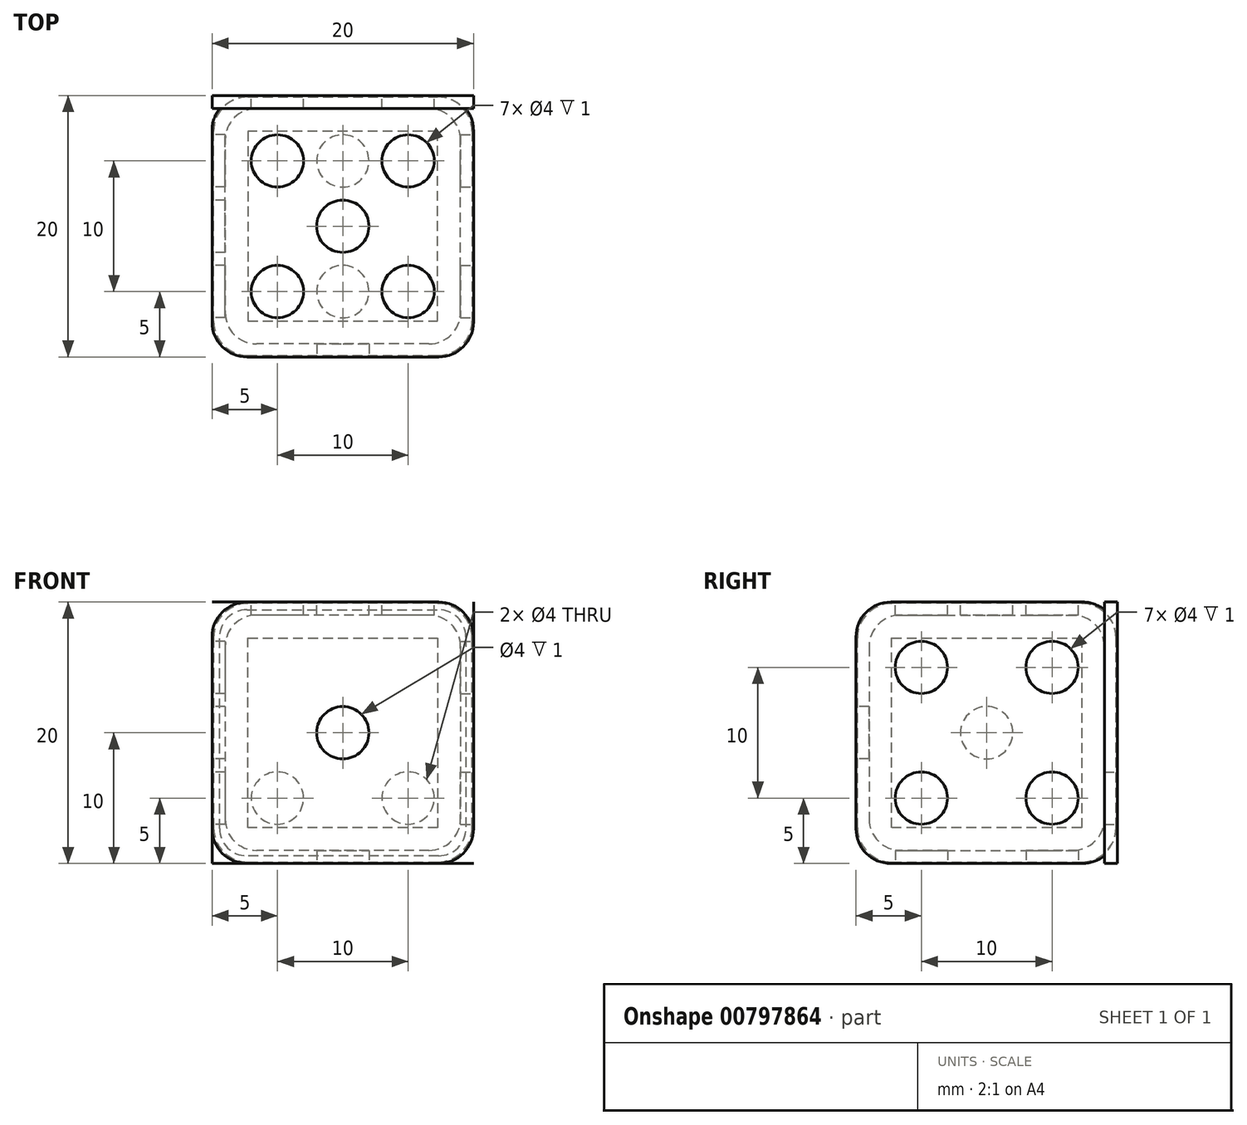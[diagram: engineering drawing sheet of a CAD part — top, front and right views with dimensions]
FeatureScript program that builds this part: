
annotation { "Feature Type Name" : "Feature", "Feature Type Description" : "" }
export const myFeature = defineFeature(function(context is Context, id is Id, definition is map)
    precondition{}
    {
        {
            assignVariable(context, id + "F0", {"variableType" : VariableType.NUMBER, "name" : "prick", "numberValue" : 4});
        }
        {
            assignVariable(context, id + "F1", {"variableType" : VariableType.LENGTH, "name" : "dist", "lengthValue" : ((getVariable(context, 'prick') + 1) * 2) * mm});
        }
        {
            var Q0;
            Q0=qCreatedBy(makeId("Top.planeOp"),FACE);
            var sketch = newSketch(context, id + "F2", { "sketchPlane" : qUnion([Q0])});
            skLineSegment(sketch, "E0.bottom", {"start": v(10, -10) * mm, "end": v(-10, -10) * mm});
            skLineSegment(sketch, "E0.top", {"start": v(10, 10) * mm, "end": v(-10, 10) * mm});
            skLineSegment(sketch, "E0.left", {"start": v(10, -10) * mm, "end": v(10, 10) * mm});
            skLineSegment(sketch, "E0.right", {"start": v(-10, -10) * mm, "end": v(-10, 10) * mm});
            skPoint(sketch, "E0.middle", {"position": v(0, 0) * mm});
            skSolve(sketch);
        }
        {
            var Q0;
            Q0=makeQuery(id+"F2.imprint","IMPRINT",FACE,{"disambiguationData":[TD([[makeQuery(id+"F2.imprint","IMPRINT",EDGE,{"derivedFrom":sQuery(id+"F2.wireOp",EDGE,"E0.bottom")}),-1.0]])]});
            extrude(context, id + "F3", {"entities" : qUnion([Q0]), "endBound" : BoundingType.SYMMETRIC, "depth" : getVariable(context, 'dist') * 2, "offsetDistance" : 25 * mm});
        }
        {
            var Q0;
            Q0=makeQuery(id+"F3.opExtrude","SWEPT_FACE",FACE,{"disambiguationData":[OSD([sQuery(id+"F2.wireOp",EDGE,"E0.bottom")])]});
            var sketch = newSketch(context, id + "F4", { "sketchPlane" : qUnion([Q0])});
            skCircle(sketch, "E1", {"center": v(0, 0) * mm, "radius": 2 * mm});
            skPoint(sketch, "E1.centerSnap0", {"position": v(10, 0) * mm});
            skSolve(sketch);
        }
        {
            var Q0;
            Q0=makeQuery(id+"F4.imprint","IMPRINT",FACE,{"disambiguationData":[TD([[makeQuery(id+"F4.imprint","IMPRINT",EDGE,{"derivedFrom":sQuery(id+"F4.wireOp",EDGE,"E1")}),1.0]])]});
            extrude(context, id + "F5", {"entities" : qUnion([Q0]), "oppositeDirection" : true, "depth" : 1 * mm, "offsetDistance" : 25 * mm});
        }
        {
            var Q0;
            Q0=makeQuery(id+"F3.opExtrude","SWEPT_FACE",FACE,{"disambiguationData":[OSD([sQuery(id+"F2.wireOp",EDGE,"E0.top")])]});
            var sketch = newSketch(context, id + "F6", { "sketchPlane" : qUnion([Q0])});
            skLineSegment(sketch, "E2", {"start": v(5, 0) * mm, "end": v(-5, 0) * mm, "construction": true});
            skPoint(sketch, "E2.startSnap0", {"position": v(10, 0) * mm});
            skPoint(sketch, "E3", {"position": v(0, 0) * mm});
            skCircle(sketch, "E4", {"center": v(-5, 0) * mm, "radius": 2 * mm});
            skCircle(sketch, "E5", {"center": v(5, 0) * mm, "radius": 2 * mm});
            skLineSegment(sketch, "E6.0.1.0", {"start": v(5, 5) * mm, "end": v(-5, 5) * mm, "construction": true});
            skCircle(sketch, "E6.0.1.1", {"center": v(-5, 5) * mm, "radius": 2 * mm});
            skCircle(sketch, "E6.0.1.2", {"center": v(5, 5) * mm, "radius": 2 * mm});
            skLineSegment(sketch, "E6.direction1", {"start": v(-5, 0) * mm, "end": v(35.29, 0) * mm, "construction": true});
            skLineSegment(sketch, "E6.direction2", {"start": v(-5, 0) * mm, "end": v(-5, 5) * mm, "construction": true});
            skCircle(sketch, "E7.MirrorC", {"center": v(5, -5) * mm, "radius": 2 * mm});
            skCircle(sketch, "E8.MirrorC", {"center": v(-5, -5) * mm, "radius": 2 * mm});
            skSolve(sketch);
        }
        {
            var Q0;
            Q0=makeQuery(id+"F6.imprint","IMPRINT",FACE,{"disambiguationData":[TD([[makeQuery(id+"F6.imprint","IMPRINT",EDGE,{"derivedFrom":sQuery(id+"F6.wireOp",EDGE,"E8.MirrorC")}),-1.0]])]});
            var Q1;
            Q1=makeQuery(id+"F6.imprint","IMPRINT",FACE,{"disambiguationData":[TD([[makeQuery(id+"F6.imprint","IMPRINT",EDGE,{"derivedFrom":sQuery(id+"F6.wireOp",EDGE,"E7.MirrorC")}),-1.0]])]});
            var Q2;
            Q2=makeQuery(id+"F6.imprint","IMPRINT",FACE,{"disambiguationData":[TD([[makeQuery(id+"F6.imprint","IMPRINT",EDGE,{"derivedFrom":sQuery(id+"F6.wireOp",EDGE,"E5")}),1.0]])]});
            var Q3;
            Q3=makeQuery(id+"F6.imprint","IMPRINT",FACE,{"disambiguationData":[TD([[makeQuery(id+"F6.imprint","IMPRINT",EDGE,{"derivedFrom":sQuery(id+"F6.wireOp",EDGE,"E4")}),1.0]])]});
            var Q4;
            Q4=makeQuery(id+"F6.imprint","IMPRINT",FACE,{"disambiguationData":[TD([[makeQuery(id+"F6.imprint","IMPRINT",EDGE,{"derivedFrom":sQuery(id+"F6.wireOp",EDGE,"E6.0.1.1")}),1.0]])]});
            var Q5;
            Q5=makeQuery(id+"F6.imprint","IMPRINT",FACE,{"disambiguationData":[TD([[makeQuery(id+"F6.imprint","IMPRINT",EDGE,{"derivedFrom":sQuery(id+"F6.wireOp",EDGE,"E6.0.1.2")}),1.0]])]});
            extrude(context, id + "F7", {"entities" : qUnion([Q0, Q1, Q2, Q3, Q4, Q5]), "oppositeDirection" : true, "depth" : 1 * mm, "offsetDistance" : 25 * mm});
        }
        {
            var Q0;
            Q0=makeQuery(id+"F3.opExtrude","CAP_EDGE",EDGE,{"disambiguationData":[OSD([sQuery(id+"F2.wireOp",EDGE,"E0.bottom")])],"isStart":true});
            var Q1;
            Q1=makeQuery(id+"F3.opExtrude","CAP_EDGE",EDGE,{"disambiguationData":[OSD([sQuery(id+"F2.wireOp",EDGE,"E0.left")])],"isStart":true});
            var Q2;
            Q2=makeQuery(id+"F3.opExtrude","CAP_EDGE",EDGE,{"disambiguationData":[OSD([sQuery(id+"F2.wireOp",EDGE,"E0.right")])],"isStart":true});
            var Q3;
            Q3=makeQuery(id+"F3.opExtrude","CAP_EDGE",EDGE,{"disambiguationData":[OSD([sQuery(id+"F2.wireOp",EDGE,"E0.top")])],"isStart":true});
            var Q4;
            Q4=makeQuery(id+"F3.opExtrude","SWEPT_EDGE",EDGE,{"disambiguationData":[OSD([sQuery(id+"F2.wireOp",EDGE,"E0.bottom"),sQuery(id+"F2.wireOp",EDGE,"E0.right")])]});
            var Q5;
            Q5=makeQuery(id+"F3.opExtrude","SWEPT_EDGE",EDGE,{"disambiguationData":[OSD([sQuery(id+"F2.wireOp",EDGE,"E0.top"),sQuery(id+"F2.wireOp",EDGE,"E0.right")])]});
            var Q6;
            Q6=makeQuery(id+"F3.opExtrude","SWEPT_EDGE",EDGE,{"disambiguationData":[OSD([sQuery(id+"F2.wireOp",EDGE,"E0.bottom"),sQuery(id+"F2.wireOp",EDGE,"E0.left")])]});
            var Q7;
            Q7=makeQuery(id+"F3.opExtrude","SWEPT_EDGE",EDGE,{"disambiguationData":[OSD([sQuery(id+"F2.wireOp",EDGE,"E0.top"),sQuery(id+"F2.wireOp",EDGE,"E0.left")])]});
            var Q8;
            Q8=makeQuery(id+"F3.opExtrude","CAP_EDGE",EDGE,{"disambiguationData":[OSD([sQuery(id+"F2.wireOp",EDGE,"E0.left")])],"isStart":false});
            var Q9;
            Q9=makeQuery(id+"F3.opExtrude","CAP_EDGE",EDGE,{"disambiguationData":[OSD([sQuery(id+"F2.wireOp",EDGE,"E0.top")])],"isStart":false});
            var Q10;
            Q10=makeQuery(id+"F3.opExtrude","CAP_EDGE",EDGE,{"disambiguationData":[OSD([sQuery(id+"F2.wireOp",EDGE,"E0.bottom")])],"isStart":false});
            var Q11;
            Q11=makeQuery(id+"F3.opExtrude","CAP_EDGE",EDGE,{"disambiguationData":[OSD([sQuery(id+"F2.wireOp",EDGE,"E0.right")])],"isStart":false});
            fillet(context, id + "F8", {"entities" : qUnion([Q0, Q1, Q2, Q3, Q4, Q5, Q6, Q7, Q8, Q9, Q10, Q11]), "tangentPropagation" : true, "radius" : (getVariable(context, 'prick') / 1.5) * mm, "defaultsChanged" : true, "vertexSettings" : [], "allowEdgeOverflow" : false});
        }
        {
            var Q0;
            Q0=makeQuery(id+"F3.opExtrude","CAP_FACE",FACE,{"disambiguationData":[OSD([sQuery(id+"F2.wireOp",EDGE,"E0.bottom"),sQuery(id+"F2.wireOp",EDGE,"E0.top"),sQuery(id+"F2.wireOp",EDGE,"E0.left"),sQuery(id+"F2.wireOp",EDGE,"E0.right")])],"isStart":false});
            var sketch = newSketch(context, id + "F9", { "sketchPlane" : qUnion([Q0])});
            skLineSegment(sketch, "E9.bottom", {"start": v(5, 5) * mm, "end": v(-5, 5) * mm, "construction": true});
            skLineSegment(sketch, "E9.top", {"start": v(5, -5) * mm, "end": v(-5, -5) * mm, "construction": true});
            skLineSegment(sketch, "E9.left", {"start": v(5, 5) * mm, "end": v(5, -5) * mm, "construction": true});
            skLineSegment(sketch, "E9.right", {"start": v(-5, 5) * mm, "end": v(-5, -5) * mm, "construction": true});
            skPoint(sketch, "E9.middle", {"position": v(0, 0) * mm});
            skCircle(sketch, "E10", {"center": v(0, 0) * mm, "radius": 2 * mm});
            skCircle(sketch, "E11", {"center": v(-5, 5) * mm, "radius": 2 * mm});
            skCircle(sketch, "E12", {"center": v(-5, -5) * mm, "radius": 2 * mm});
            skCircle(sketch, "E13", {"center": v(5, -5) * mm, "radius": 2 * mm});
            skCircle(sketch, "E14", {"center": v(5, 5) * mm, "radius": 2 * mm});
            skSolve(sketch);
        }
        {
            var Q0;
            Q0 = qSketchRegion(id + "F9", true);
            extrude(context, id + "F10", {"entities" : qUnion([Q0]), "oppositeDirection" : true, "depth" : 1 * mm, "offsetDistance" : 25 * mm});
        }
        {
            var Q0;
            Q0=makeQuery(id+"F3.opExtrude","CAP_FACE",FACE,{"disambiguationData":[OSD([sQuery(id+"F2.wireOp",EDGE,"E0.bottom"),sQuery(id+"F2.wireOp",EDGE,"E0.top"),sQuery(id+"F2.wireOp",EDGE,"E0.left"),sQuery(id+"F2.wireOp",EDGE,"E0.right")])],"isStart":true});
            var sketch = newSketch(context, id + "F11", { "sketchPlane" : qUnion([Q0])});
            skLineSegment(sketch, "E15", {"start": v(0, -5) * mm, "end": v(0, 5) * mm});
            skCircle(sketch, "E16", {"center": v(0, -5) * mm, "radius": 2 * mm});
            skCircle(sketch, "E17", {"center": v(0, 5) * mm, "radius": 2 * mm});
            skSolve(sketch);
        }
        {
            var Q0;
            Q0=makeQuery(id+"F11.imprint","IMPRINT",FACE,{"disambiguationData":[TD([[makeQuery(id+"F11.imprint","IMPRINT",EDGE,{"derivedFrom":sQuery(id+"F11.wireOp",EDGE,"E16")}),1.0]])]});
            var Q1;
            Q1=makeQuery(id+"F11.imprint","IMPRINT",FACE,{"disambiguationData":[TD([[makeQuery(id+"F11.imprint","IMPRINT",EDGE,{"derivedFrom":sQuery(id+"F11.wireOp",EDGE,"E17")}),1.0]])]});
            extrude(context, id + "F12", {"entities" : qUnion([Q0, Q1]), "oppositeDirection" : true, "depth" : 1 * mm, "offsetDistance" : 25 * mm});
        }
        {
            var Q0;
            Q0=makeQuery(id+"F3.opExtrude","SWEPT_FACE",FACE,{"disambiguationData":[OSD([sQuery(id+"F2.wireOp",EDGE,"E0.right")])]});
            var sketch = newSketch(context, id + "F13", { "sketchPlane" : qUnion([Q0])});
            skLineSegment(sketch, "E18.bottom", {"start": v(5, 5) * mm, "end": v(-5, 5) * mm, "construction": true});
            skLineSegment(sketch, "E18.top", {"start": v(5, -5) * mm, "end": v(-5, -5) * mm, "construction": true});
            skLineSegment(sketch, "E18.left", {"start": v(5, 5) * mm, "end": v(5, -5) * mm, "construction": true});
            skLineSegment(sketch, "E18.right", {"start": v(-5, 5) * mm, "end": v(-5, -5) * mm, "construction": true});
            skPoint(sketch, "E18.middle", {"position": v(0, 0) * mm});
            skPoint(sketch, "E18.middle.positionSnap0", {"position": v(-7.33, 0) * mm});
            skPoint(sketch, "E18.centerSnap0", {"position": v(-7.33, 0) * mm});
            skCircle(sketch, "E19", {"center": v(0, 0) * mm, "radius": 2 * mm});
            skCircle(sketch, "E20", {"center": v(5, 5) * mm, "radius": 2 * mm});
            skCircle(sketch, "E21", {"center": v(-5, -5) * mm, "radius": 2 * mm});
            skSolve(sketch);
        }
        {
            var Q0;
            Q0=makeQuery(id+"F3.opExtrude","SWEPT_FACE",FACE,{"disambiguationData":[OSD([sQuery(id+"F2.wireOp",EDGE,"E0.left")])]});
            var sketch = newSketch(context, id + "F14", { "sketchPlane" : qUnion([Q0])});
            skLineSegment(sketch, "E22.bottom", {"start": v(5, -5) * mm, "end": v(-5, -5) * mm, "construction": true});
            skLineSegment(sketch, "E22.top", {"start": v(5, 5) * mm, "end": v(-5, 5) * mm, "construction": true});
            skLineSegment(sketch, "E22.left", {"start": v(5, -5) * mm, "end": v(5, 5) * mm, "construction": true});
            skLineSegment(sketch, "E22.right", {"start": v(-5, -5) * mm, "end": v(-5, 5) * mm, "construction": true});
            skPoint(sketch, "E22.middle", {"position": v(0, 0) * mm});
            skPoint(sketch, "E22.middle.positionSnap0", {"position": v(7.33, 0) * mm});
            skPoint(sketch, "E22.centerSnap0", {"position": v(7.33, 0) * mm});
            skCircle(sketch, "E23", {"center": v(5, 5) * mm, "radius": 2 * mm});
            skCircle(sketch, "E24", {"center": v(5, -5) * mm, "radius": 2 * mm});
            skCircle(sketch, "E25", {"center": v(-5, -5) * mm, "radius": 2 * mm});
            skCircle(sketch, "E26", {"center": v(-5, 5) * mm, "radius": 2 * mm});
            skSolve(sketch);
        }
        {
            var Q0;
            Q0 = qSketchRegion(id + "F13", true);
            extrude(context, id + "F15", {"entities" : qUnion([Q0]), "oppositeDirection" : true, "depth" : 1 * mm, "offsetDistance" : 25 * mm});
        }
        {
            var Q0;
            Q0 = qSketchRegion(id + "F14", true);
            extrude(context, id + "F16", {"entities" : qUnion([Q0]), "oppositeDirection" : true, "depth" : 1 * mm, "offsetDistance" : 25 * mm});
        }
        {
            var Q0;
            Q0=makeQuery(id+"F3.opExtrude","SWEPT_BODY",BODY,{"disambiguationData":[OSD([sQuery(id+"F2.wireOp",EDGE,"E0.bottom"),sQuery(id+"F2.wireOp",EDGE,"E0.top"),sQuery(id+"F2.wireOp",EDGE,"E0.left"),sQuery(id+"F2.wireOp",EDGE,"E0.right")])]});
            var Q1;
            Q1=qCreatedBy(makeId("Origin.pointOp"),VERTEX);
            transform(context, id + "F17", {"entities" : qUnion([Q0]), "transformType" : TransformType.SCALE_UNIFORMLY, "scale" : 0.99, "scalePoint" : qUnion([Q1]), "makeCopy" : true});
        }
        {
            var Q0;
            Q0=makeQuery(id+"F17.opPattern","COPY",BODY,{"derivedFrom":makeQuery(id+"F3.opExtrude","SWEPT_BODY",BODY,{"disambiguationData":[OSD([sQuery(id+"F2.wireOp",EDGE,"E0.bottom"),sQuery(id+"F2.wireOp",EDGE,"E0.top"),sQuery(id+"F2.wireOp",EDGE,"E0.left"),sQuery(id+"F2.wireOp",EDGE,"E0.right")])]}),"instanceName":"1"});
            var Q1;
            Q1=qCreatedBy(makeId("Origin.pointOp"),VERTEX);
            transform(context, id + "F18", {"entities" : qUnion([Q0]), "transformType" : TransformType.SCALE_UNIFORMLY, "scale" : 1, "scalePoint" : qUnion([Q1]), "makeCopy" : true});
        }
        {
            var Q0;
            Q0=makeQuery(id+"F3.opExtrude","SWEPT_BODY",BODY,{"disambiguationData":[OSD([sQuery(id+"F2.wireOp",EDGE,"E0.bottom"),sQuery(id+"F2.wireOp",EDGE,"E0.top"),sQuery(id+"F2.wireOp",EDGE,"E0.left"),sQuery(id+"F2.wireOp",EDGE,"E0.right")])]});
            var Q1;
            Q1=qCreatedBy(makeId("Origin.pointOp"),VERTEX);
            transform(context, id + "F19", {"entities" : qUnion([Q0]), "transformType" : TransformType.SCALE_UNIFORMLY, "scale" : 0.9, "scalePoint" : qUnion([Q1]), "makeCopy" : true});
        }
        {
            var Q0;
            Q0=makeQuery(id+"F5.opExtrude","SWEPT_BODY",BODY,{"disambiguationData":[OSD([sQuery(id+"F4.wireOp",EDGE,"E1")])]});
            var Q1;
            Q1=makeQuery(id+"F7.opExtrude","SWEPT_BODY",BODY,{"disambiguationData":[OSD([sQuery(id+"F6.wireOp",EDGE,"E4")])]});
            var Q2;
            Q2=makeQuery(id+"F7.opExtrude","SWEPT_BODY",BODY,{"disambiguationData":[OSD([sQuery(id+"F6.wireOp",EDGE,"E5")])]});
            var Q3;
            Q3=makeQuery(id+"F7.opExtrude","SWEPT_BODY",BODY,{"disambiguationData":[OSD([sQuery(id+"F6.wireOp",EDGE,"E6.0.1.1")])]});
            var Q4;
            Q4=makeQuery(id+"F7.opExtrude","SWEPT_BODY",BODY,{"disambiguationData":[OSD([sQuery(id+"F6.wireOp",EDGE,"E6.0.1.2")])]});
            var Q5;
            Q5=makeQuery(id+"F7.opExtrude","SWEPT_BODY",BODY,{"disambiguationData":[OSD([sQuery(id+"F6.wireOp",EDGE,"E7.MirrorC")])]});
            var Q6;
            Q6=makeQuery(id+"F7.opExtrude","SWEPT_BODY",BODY,{"disambiguationData":[OSD([sQuery(id+"F6.wireOp",EDGE,"E8.MirrorC")])]});
            var Q7;
            Q7=makeQuery(id+"F10.opExtrude","SWEPT_BODY",BODY,{"disambiguationData":[OSD([sQuery(id+"F9.wireOp",EDGE,"E10")])]});
            var Q8;
            Q8=makeQuery(id+"F10.opExtrude","SWEPT_BODY",BODY,{"disambiguationData":[OSD([sQuery(id+"F9.wireOp",EDGE,"E11")])]});
            var Q9;
            Q9=makeQuery(id+"F10.opExtrude","SWEPT_BODY",BODY,{"disambiguationData":[OSD([sQuery(id+"F9.wireOp",EDGE,"E12")])]});
            var Q10;
            Q10=makeQuery(id+"F10.opExtrude","SWEPT_BODY",BODY,{"disambiguationData":[OSD([sQuery(id+"F9.wireOp",EDGE,"E13")])]});
            var Q11;
            Q11=makeQuery(id+"F10.opExtrude","SWEPT_BODY",BODY,{"disambiguationData":[OSD([sQuery(id+"F9.wireOp",EDGE,"E14")])]});
            var Q12;
            Q12=makeQuery(id+"F12.opExtrude","SWEPT_BODY",BODY,{"disambiguationData":[OSD([sQuery(id+"F11.wireOp",EDGE,"E16")])]});
            var Q13;
            Q13=makeQuery(id+"F12.opExtrude","SWEPT_BODY",BODY,{"disambiguationData":[OSD([sQuery(id+"F11.wireOp",EDGE,"E17")])]});
            var Q14;
            Q14=makeQuery(id+"F15.opExtrude","SWEPT_BODY",BODY,{"disambiguationData":[OSD([sQuery(id+"F13.wireOp",EDGE,"E19")])]});
            var Q15;
            Q15=makeQuery(id+"F15.opExtrude","SWEPT_BODY",BODY,{"disambiguationData":[OSD([sQuery(id+"F13.wireOp",EDGE,"E20")])]});
            var Q16;
            Q16=makeQuery(id+"F15.opExtrude","SWEPT_BODY",BODY,{"disambiguationData":[OSD([sQuery(id+"F13.wireOp",EDGE,"E21")])]});
            var Q17;
            Q17=makeQuery(id+"F16.opExtrude","SWEPT_BODY",BODY,{"disambiguationData":[OSD([sQuery(id+"F14.wireOp",EDGE,"E23")])]});
            var Q18;
            Q18=makeQuery(id+"F16.opExtrude","SWEPT_BODY",BODY,{"disambiguationData":[OSD([sQuery(id+"F14.wireOp",EDGE,"E24")])]});
            var Q19;
            Q19=makeQuery(id+"F16.opExtrude","SWEPT_BODY",BODY,{"disambiguationData":[OSD([sQuery(id+"F14.wireOp",EDGE,"E25")])]});
            var Q20;
            Q20=makeQuery(id+"F16.opExtrude","SWEPT_BODY",BODY,{"disambiguationData":[OSD([sQuery(id+"F14.wireOp",EDGE,"E26")])]});
            var Q21;
            Q21=makeQuery(id+"F3.opExtrude","SWEPT_BODY",BODY,{"disambiguationData":[OSD([sQuery(id+"F2.wireOp",EDGE,"E0.bottom"),sQuery(id+"F2.wireOp",EDGE,"E0.top"),sQuery(id+"F2.wireOp",EDGE,"E0.left"),sQuery(id+"F2.wireOp",EDGE,"E0.right")])]});
            booleanBodies(context, id + "F20", {"operationType" : BooleanOperationType.SUBTRACTION, "tools" : qUnion([Q0, Q1, Q2, Q3, Q4, Q5, Q6, Q7, Q8, Q9, Q10, Q11, Q12, Q13, Q14, Q15, Q16, Q17, Q18, Q19, Q20]), "targets" : qUnion([Q21]), "keepTools" : true});
        }
        {
            var Q0;
            Q0=makeQuery(id+"F18.opPattern","COPY",BODY,{"derivedFrom":makeQuery(id+"F17.opPattern","COPY",BODY,{"derivedFrom":makeQuery(id+"F3.opExtrude","SWEPT_BODY",BODY,{"disambiguationData":[OSD([sQuery(id+"F2.wireOp",EDGE,"E0.bottom"),sQuery(id+"F2.wireOp",EDGE,"E0.top"),sQuery(id+"F2.wireOp",EDGE,"E0.left"),sQuery(id+"F2.wireOp",EDGE,"E0.right")])]}),"instanceName":"1"}),"instanceName":"1"});
            var Q1;
            Q1=makeQuery(id+"F17.opPattern","COPY",BODY,{"derivedFrom":makeQuery(id+"F3.opExtrude","SWEPT_BODY",BODY,{"disambiguationData":[OSD([sQuery(id+"F2.wireOp",EDGE,"E0.bottom"),sQuery(id+"F2.wireOp",EDGE,"E0.top"),sQuery(id+"F2.wireOp",EDGE,"E0.left"),sQuery(id+"F2.wireOp",EDGE,"E0.right")])]}),"instanceName":"1"});
            booleanBodies(context, id + "F21", {"operationType" : BooleanOperationType.SUBTRACTION, "tools" : qUnion([Q0]), "targets" : qUnion([Q1])});
        }
    });
